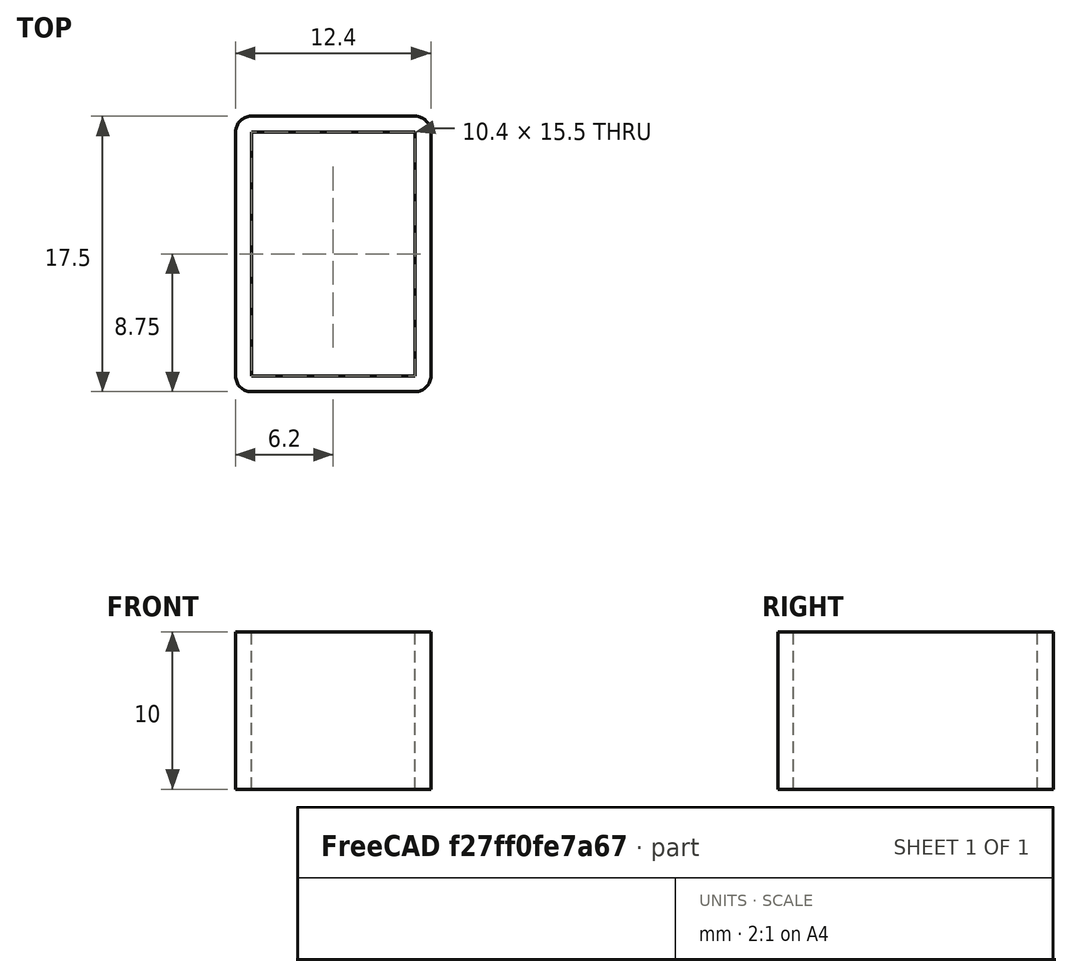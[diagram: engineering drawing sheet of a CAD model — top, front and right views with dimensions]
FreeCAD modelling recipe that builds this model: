
FCSTD DOCUMENT  (FreeCAD 2024.2R37179 (Git))
Label: Joints
License: All rights reserved
LicenseURL: https://en.wikipedia.org/wiki/All_rights_reserved
objects: Sketcher::SketchObject×1, Spreadsheet::Sheet×1, PartDesign::Pad×1, PartDesign::Body×1
note: 4 computed .brp shape members not serialized (recipe doc carries the construction recipe); baked Part::Feature solids carry a one-line shape summary decoded from their .brp

FEATURE [Sketcher::SketchObject] Sketch
  AttachmentSupport = -> [XY_Plane]
  FullyConstrained = true
  MapMode = 5
  expr: Constraints[10] = Spreadsheet.width
  expr: Constraints[33] = Spreadsheet.height + Spreadsheet.thickness
  expr: Constraints[34] = Spreadsheet.width + Spreadsheet.thickness
  expr: Constraints[35] = Spreadsheet.diameter
  expr: Constraints[9] = Spreadsheet.height
  sketch-geometry (16):
    g0: LineSegment StartX=-5.2 StartY=-7.75 StartZ=0 EndX=5.2 EndY=-7.75 EndZ=0
    g1: LineSegment StartX=5.2 StartY=-7.75 StartZ=0 EndX=5.2 EndY=7.75 EndZ=0
    g2: LineSegment StartX=5.2 StartY=7.75 StartZ=0 EndX=-5.2 EndY=7.75 EndZ=0
    g3: LineSegment StartX=-5.2 StartY=7.75 StartZ=0 EndX=-5.2 EndY=-7.75 EndZ=0
    g4: GeomPoint X=0 Y=0 Z=0
    g5: LineSegment StartX=-6.2 StartY=7.75 StartZ=0 EndX=-6.2 EndY=-7.75 EndZ=0
    g6: LineSegment StartX=-5.2 StartY=-8.75 StartZ=0 EndX=5.2 EndY=-8.75 EndZ=0
    g7: LineSegment StartX=6.2 StartY=-7.75 StartZ=0 EndX=6.2 EndY=7.75 EndZ=0
    g8: LineSegment StartX=5.2 StartY=8.75 StartZ=0 EndX=-5.2 EndY=8.75 EndZ=0
    g9: ArcOfCircle CenterX=-5.2 CenterY=7.75 CenterZ=0 NormalX=0 NormalY=0 NormalZ=1 AngleXU=0 Radius=1 StartAngle=1.5708 EndAngle=3.14159
    g10: ArcOfCircle CenterX=-5.2 CenterY=-7.75 CenterZ=0 NormalX=0 NormalY=0 NormalZ=1 AngleXU=0 Radius=1 StartAngle=3.14159 EndAngle=4.71239
    g11: ArcOfCircle CenterX=5.2 CenterY=-7.75 CenterZ=0 NormalX=0 NormalY=0 NormalZ=1 AngleXU=0 Radius=1 StartAngle=4.71239 EndAngle=6.28319
    g12: ArcOfCircle CenterX=5.2 CenterY=7.75 CenterZ=0 NormalX=0 NormalY=0 NormalZ=1 AngleXU=0 Radius=1 StartAngle=2e-16 EndAngle=1.5708
    g13: GeomPoint X=-6.2 Y=8.75 Z=0
    g14: GeomPoint X=6.2 Y=-8.75 Z=0
    g15: GeomPoint X=0 Y=0 Z=0
  constraints (36):
    c: Coincident(g0,g1)
    c: Coincident(g1,g2)
    c: Coincident(g2,g3)
    c: Coincident(g3,g0)
    c: Horizontal(g0)
    c: Horizontal(g2)
    c: Vertical(g1)
    c: Vertical(g3)
    c: Symmetric(g2,g0,g4)
    c: Distance(g1,g3) = 10.4
    c: Distance(g0,g2) = 15.5
    c: Coincident(g4,g-1)
    c: Tangent(g5,g9) = -1.5708
    c: Tangent(g5,g10) = -1.5708
    c: Tangent(g6,g10) = -1.5708
    c: Tangent(g6,g11) = -1.5708
    c: Tangent(g7,g11) = -1.5708
    c: Tangent(g7,g12) = -1.5708
    c: Tangent(g8,g12) = -1.5708
    c: Tangent(g8,g9) = -1.5708
    c: Vertical(g5)
    c: Vertical(g7)
    c: Horizontal(g6)
    c: Horizontal(g8)
    c: Equal(g9,g10)
    c: Equal(g10,g11)
    c: Equal(g11,g12)
    c: PointOnObject(g13,g5)
    c: PointOnObject(g13,g8)
    c: PointOnObject(g14,g6)
    c: PointOnObject(g14,g7)
    c: Symmetric(g6,g8,g15)
    c: Coincident(g15,g4)
    c: Distance(g5,g7) = 12.4
    c: DistanceY(g6,g8) = 17.5
    c: Diameter(g12) = 2
FEATURE [Spreadsheet::Sheet] Spreadsheet
  cells = A1='width; B1(width)=15.5; A2='height; B2(height)=10.4; A3='thickness; B3(thickness)=2; A4='diameter; B4(diameter)=2
FEATURE [PartDesign::Pad] Pad
  Direction = (0,0,1)
  Length = 10
  Length2 = 10
  Profile = -> Sketch
  ReferenceAxis = -> Sketch [N_Axis]
  Refine = true
  Suppressed = false
  Type = 0
FEATURE [PartDesign::Body] Body
  Group = -> [Sketch,Pad]
  Origin = -> Origin
  Tip = -> Pad
